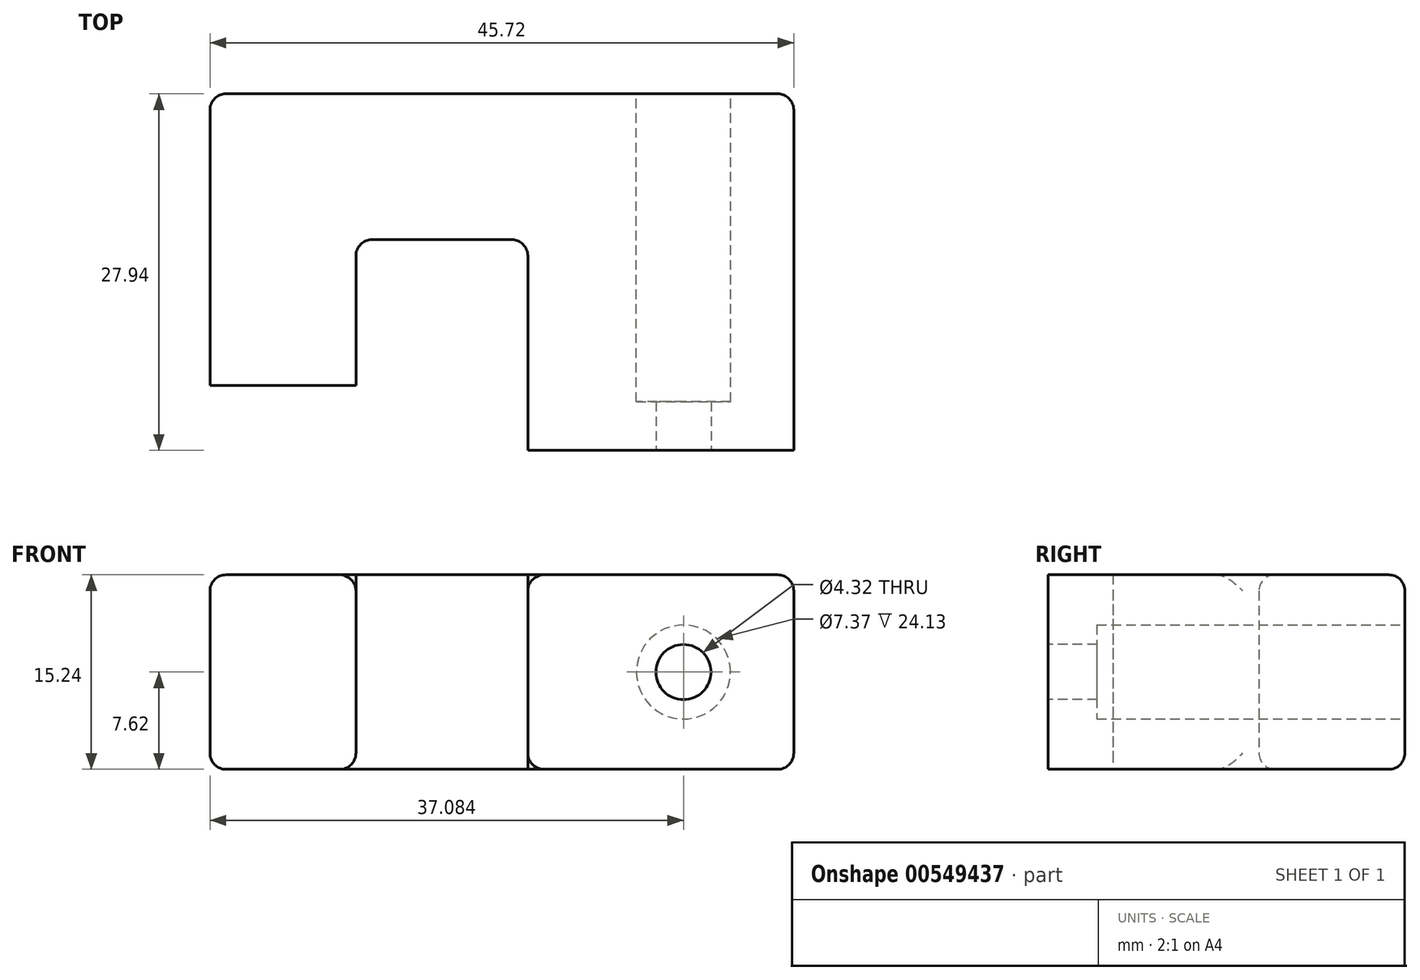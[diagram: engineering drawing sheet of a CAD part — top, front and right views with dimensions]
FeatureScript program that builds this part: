
annotation { "Feature Type Name" : "Feature", "Feature Type Description" : "" }
export const myFeature = defineFeature(function(context is Context, id is Id, definition is map)
    precondition{}
    {
        {
            var Q0;
            Q0=qCreatedBy(makeId("Top.planeOp"),FACE);
            var sketch = newSketch(context, id + "F0", { "sketchPlane" : qUnion([Q0])});
            skLineSegment(sketch, "E0", {"start": v(0, 0) * mm, "end": v(-11.43, 0) * mm});
            skLineSegment(sketch, "E1", {"start": v(-11.43, 0) * mm, "end": v(-11.43, 22.86) * mm});
            skLineSegment(sketch, "E2", {"start": v(-11.43, 22.86) * mm, "end": v(34.3, 22.86) * mm});
            skLineSegment(sketch, "E3", {"start": v(34.3, 22.86) * mm, "end": v(34.3, -5.08) * mm});
            skLineSegment(sketch, "E4", {"start": v(34.3, -5.08) * mm, "end": v(13.46, -5.08) * mm});
            skLineSegment(sketch, "E5", {"start": v(13.46, -5.08) * mm, "end": v(13.46, 11.43) * mm});
            skLineSegment(sketch, "E6", {"start": v(13.46, 11.43) * mm, "end": v(0, 11.43) * mm});
            skLineSegment(sketch, "E7", {"start": v(0, 11.43) * mm, "end": v(0, 0) * mm});
            skSolve(sketch);
        }
        {
            var Q0;
            Q0 = qSketchRegion(id + "F0", true);
            extrude(context, id + "F1", {"entities" : qUnion([Q0]), "depth" : 15.24 * mm, "offsetDistance" : 25.4 * mm});
        }
        {
            var Q0;
            Q0=makeQuery(id+"F1.opExtrude","SWEPT_FACE",FACE,{"disambiguationData":[OSD([sQuery(id+"F0.wireOp",EDGE,"E4")])]});
            var sketch = newSketch(context, id + "F2", { "sketchPlane" : qUnion([Q0])});
            skCircle(sketch, "E8", {"center": v(25.65, 7.62) * mm, "radius": 2.16 * mm});
            skPoint(sketch, "E9", {"position": v(34.3, 7.62) * mm});
            skSolve(sketch);
        }
        {
            var Q0;
            Q0 = qSketchRegion(id + "F2", true);
            var Q1;
            Q1=makeQuery(id+"F1.opExtrude","SWEPT_FACE",FACE,{"disambiguationData":[OSD([sQuery(id+"F0.wireOp",EDGE,"E2")])]});
            extrude(context, id + "F3", {"entities" : qUnion([Q0]), "operationType" : NewBodyOperationType.REMOVE, "endBound" : BoundingType.UP_TO_SURFACE, "oppositeDirection" : true, "depth" : 25.4 * mm, "endBoundEntityFace" : qUnion([Q1]), "offsetDistance" : 25.4 * mm});
        }
        {
            var Q0;
            Q0=makeQuery(id+"F1.opExtrude","SWEPT_FACE",FACE,{"disambiguationData":[OSD([sQuery(id+"F0.wireOp",EDGE,"E2")])]});
            var sketch = newSketch(context, id + "F4", { "sketchPlane" : qUnion([Q0])});
            skCircle(sketch, "E10", {"center": v(-25.65, 7.62) * mm, "radius": 3.68 * mm});
            skSolve(sketch);
        }
        {
            var Q0;
            Q0 = qSketchRegion(id + "F4", true);
            extrude(context, id + "F5", {"entities" : qUnion([Q0]), "operationType" : NewBodyOperationType.REMOVE, "oppositeDirection" : true, "depth" : 24.13 * mm, "offsetDistance" : 25.4 * mm});
        }
        {
            var Q0;
            Q0=makeQuery(id+"F1.opExtrude","SWEPT_EDGE",EDGE,{"disambiguationData":[OSD([sQuery(id+"F0.wireOp",EDGE,"E6"),sQuery(id+"F0.wireOp",EDGE,"E7")])]});
            var Q1;
            Q1=makeQuery(id+"F1.opExtrude","SWEPT_EDGE",EDGE,{"disambiguationData":[OSD([sQuery(id+"F0.wireOp",EDGE,"E5"),sQuery(id+"F0.wireOp",EDGE,"E6")])]});
            var Q2;
            Q2=makeQuery(id+"F1.opExtrude","CAP_EDGE",EDGE,{"disambiguationData":[OSD([sQuery(id+"F0.wireOp",EDGE,"E6")])],"isStart":false});
            var Q3;
            Q3=makeQuery(id+"F1.opExtrude","CAP_EDGE",EDGE,{"disambiguationData":[OSD([sQuery(id+"F0.wireOp",EDGE,"E7")])],"isStart":true});
            var Q4;
            Q4=makeQuery(id+"F1.opExtrude","SWEPT_EDGE",EDGE,{"disambiguationData":[OSD([sQuery(id+"F0.wireOp",EDGE,"E1"),sQuery(id+"F0.wireOp",EDGE,"E2")])]});
            var Q5;
            Q5=makeQuery(id+"F1.opExtrude","CAP_EDGE",EDGE,{"disambiguationData":[OSD([sQuery(id+"F0.wireOp",EDGE,"E1")])],"isStart":false});
            var Q6;
            Q6=makeQuery(id+"F1.opExtrude","CAP_EDGE",EDGE,{"disambiguationData":[OSD([sQuery(id+"F0.wireOp",EDGE,"E1")])],"isStart":true});
            var Q7;
            Q7=makeQuery(id+"F1.opExtrude","CAP_EDGE",EDGE,{"disambiguationData":[OSD([sQuery(id+"F0.wireOp",EDGE,"E2")])],"isStart":false});
            var Q8;
            Q8=makeQuery(id+"F1.opExtrude","SWEPT_EDGE",EDGE,{"disambiguationData":[OSD([sQuery(id+"F0.wireOp",EDGE,"E2"),sQuery(id+"F0.wireOp",EDGE,"E3")])]});
            var Q9;
            Q9=makeQuery(id+"F1.opExtrude","CAP_EDGE",EDGE,{"disambiguationData":[OSD([sQuery(id+"F0.wireOp",EDGE,"E3")])],"isStart":false});
            var Q10;
            Q10=makeQuery(id+"F1.opExtrude","CAP_EDGE",EDGE,{"disambiguationData":[OSD([sQuery(id+"F0.wireOp",EDGE,"E3")])],"isStart":true});
            var Q11;
            Q11=makeQuery(id+"F1.opExtrude","CAP_EDGE",EDGE,{"disambiguationData":[OSD([sQuery(id+"F0.wireOp",EDGE,"E2")])],"isStart":true});
            var Q12;
            Q12=makeQuery(id+"F5.boolean.opBoolean","COPY",EDGE,{"derivedFrom":makeQuery(id+"F5.opExtrude","CAP_EDGE",EDGE,{"disambiguationData":[OSD([sQuery(id+"F4.wireOp",EDGE,"E10")])],"isStart":true})});
            var Q13;
            Q13=makeQuery(id+"F1.opExtrude","CAP_EDGE",EDGE,{"disambiguationData":[OSD([sQuery(id+"F0.wireOp",EDGE,"E6")])],"isStart":true});
            fillet(context, id + "F6", {"entities" : qUnion([Q0, Q1, Q2, Q3, Q4, Q5, Q6, Q7, Q8, Q9, Q10, Q11, Q12, Q13]), "radius" : 1.27 * mm, "tangentPropagation" : true, "allowEdgeOverflow" : false});
        }
    });
